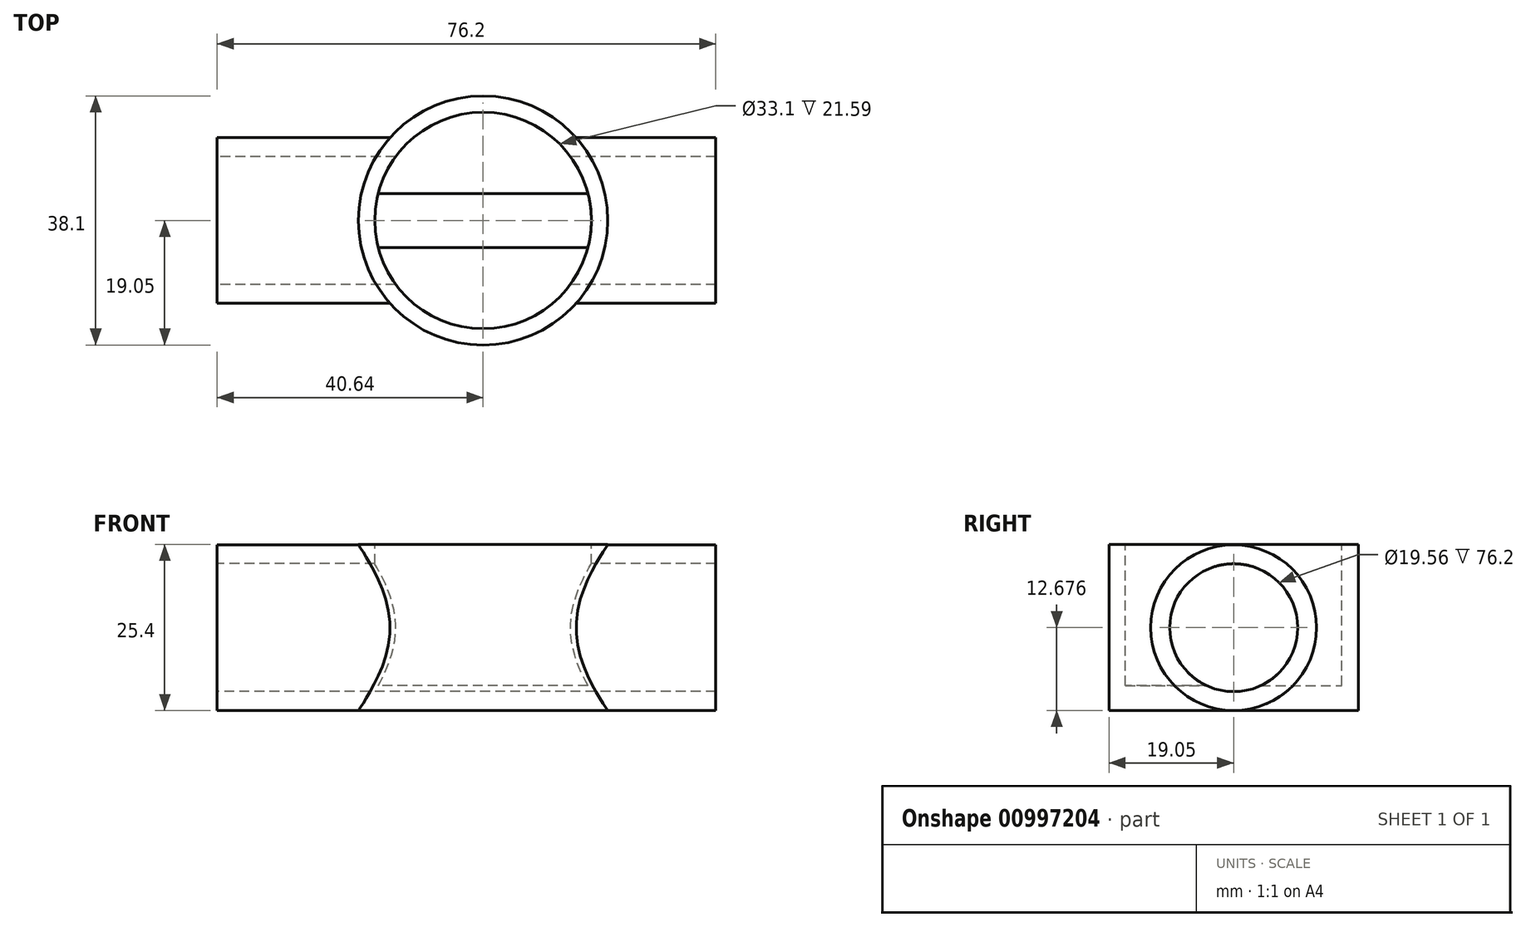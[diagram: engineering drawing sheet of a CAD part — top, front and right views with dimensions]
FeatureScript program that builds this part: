
annotation { "Feature Type Name" : "Feature", "Feature Type Description" : "" }
export const myFeature = defineFeature(function(context is Context, id is Id, definition is map)
    precondition{}
    {
        {
            var Q0;
            Q0=qCreatedBy(makeId("Top.planeOp"),FACE);
            var sketch = newSketch(context, id + "F0", { "sketchPlane" : qUnion([Q0])});
            skCircle(sketch, "E0", {"center": v(0, 0) * mm, "radius": 19.05 * mm});
            skSolve(sketch);
        }
        {
            var Q0;
            Q0=makeQuery(id+"F0.imprint","IMPRINT",FACE,{"disambiguationData":[TD([[makeQuery(id+"F0.imprint","IMPRINT",EDGE,{"derivedFrom":sQuery(id+"F0.wireOp",EDGE,"E0")}),1.0]])]});
            extrude(context, id + "F1", {"entities" : qUnion([Q0]), "depth" : 25.4 * mm, "offsetDistance" : 25.4 * mm});
        }
        {
            var Q0;
            Q0=qCreatedBy(makeId("Right.planeOp"),FACE);
            var sketch = newSketch(context, id + "F2", { "sketchPlane" : qUnion([Q0])});
            skLineSegment(sketch, "E1", {"start": v(0, 0) * mm, "end": v(0, 25.35) * mm});
            skLineSegment(sketch, "E2", {"start": v(0, 25.35) * mm, "end": v(0, 12.68) * mm});
            skCircle(sketch, "E3", {"center": v(0, 12.68) * mm, "radius": 12.68 * mm});
            skCircle(sketch, "E4", {"center": v(0, 12.68) * mm, "radius": 9.78 * mm});
            skSolve(sketch);
        }
        {
            var Q0;
            Q0 = qSketchRegion(id + "F2", true);
            extrude(context, id + "F3", {"entities" : qUnion([Q0]), "operationType" : NewBodyOperationType.ADD, "depth" : 35.56 * mm, "offsetDistance" : 25.4 * mm, "hasSecondDirection" : true, "secondDirectionOppositeDirection" : true, "secondDirectionDepth" : 40.64 * mm});
        }
        {
            var Q0;
            Q0=makeQuery(id+"F3.opExtrude","CAP_FACE",FACE,{"disambiguationData":[OSD([sQuery(id+"F2.wireOp",EDGE,"E3"),sQuery(id+"F2.wireOp",EDGE,"E4")])],"isStart":false});
            var sketch = newSketch(context, id + "F4", { "sketchPlane" : qUnion([Q0])});
            skCircle(sketch, "E5", {"center": v(0, 12.68) * mm, "radius": 9.78 * mm});
            skPoint(sketch, "E5.first.point", {"position": v(5.27, 4.44) * mm});
            skPoint(sketch, "E5.second.point", {"position": v(-9.15, 9.22) * mm});
            skPoint(sketch, "E5.third.point", {"position": v(7.5, 18.96) * mm});
            skSolve(sketch);
        }
        {
            var Q0;
            Q0 = qSketchRegion(id + "F4", true);
            extrude(context, id + "F5", {"entities" : qUnion([Q0]), "operationType" : NewBodyOperationType.REMOVE, "oppositeDirection" : true, "depth" : 73.15 * mm, "offsetDistance" : 25.4 * mm});
        }
        {
            var Q0;
            Q0=makeQuery(id+"F1.opExtrude","CAP_FACE",FACE,{"disambiguationData":[OSD([sQuery(id+"F0.wireOp",EDGE,"E0")])],"isStart":false});
            var sketch = newSketch(context, id + "F6", { "sketchPlane" : qUnion([Q0])});
            skCircle(sketch, "E6", {"center": v(0, 0) * mm, "radius": 16.55 * mm});
            skSolve(sketch);
        }
        {
            var Q0;
            Q0=makeQuery(id+"F6.imprint","IMPRINT",FACE,{"disambiguationData":[TD([[makeQuery(id+"F6.imprint","IMPRINT",EDGE,{"derivedFrom":sQuery(id+"F6.wireOp",EDGE,"E6")}),1.0]])]});
            extrude(context, id + "F7", {"entities" : qUnion([Q0]), "operationType" : NewBodyOperationType.REMOVE, "oppositeDirection" : true, "depth" : 21.59 * mm, "offsetDistance" : 25.4 * mm});
        }
    });
